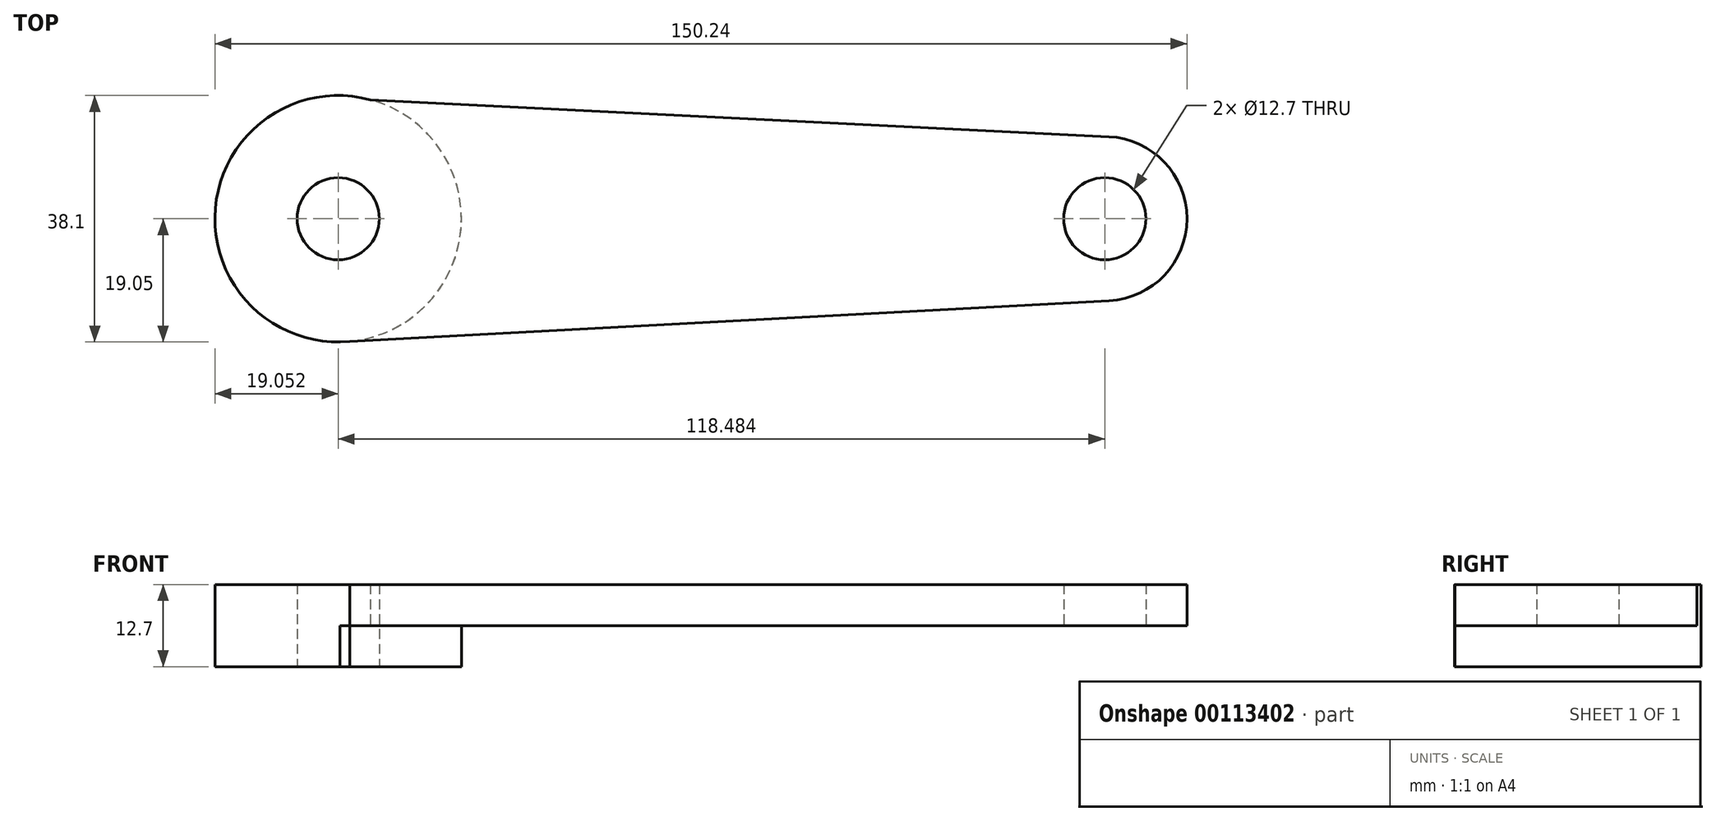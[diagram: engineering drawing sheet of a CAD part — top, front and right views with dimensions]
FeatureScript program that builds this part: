
annotation { "Feature Type Name" : "Feature", "Feature Type Description" : "" }
export const myFeature = defineFeature(function(context is Context, id is Id, definition is map)
    precondition{}
    {
        {
            var Q0;
            Q0=qCreatedBy(makeId("Top.planeOp"),FACE);
            var sketch = newSketch(context, id + "F0", { "sketchPlane" : qUnion([Q0])});
            skCircle(sketch, "E0", {"center": v(62.32, 0) * mm, "radius": 12.7 * mm});
            skCircle(sketch, "E1", {"center": v(-56.17, 0) * mm, "radius": 19.05 * mm});
            skLineSegment(sketch, "E2", {"start": v(-51.2, 18.4) * mm, "end": v(62.95, 12.68) * mm});
            skLineSegment(sketch, "E3", {"start": v(-55.91, -19.05) * mm, "end": v(63, -12.68) * mm});
            skCircle(sketch, "E4", {"center": v(-56.17, 0) * mm, "radius": 6.35 * mm});
            skCircle(sketch, "E5", {"center": v(62.32, 0) * mm, "radius": 6.35 * mm});
            skCircle(sketch, "E6", {"center": v(62.32, 0) * mm, "radius": 3.18 * mm});
            skCircle(sketch, "E7", {"center": v(-56.17, 0) * mm, "radius": 3.18 * mm});
            skSolve(sketch);
        }
        {
            var Q0;
            {var subQ0=sQuery(id+"F0.wireOp",EDGE,"E1");var subQ1=makeQuery(id+"F0.imprint","INTERSECT",VERTEX,{"derivedFrom":[subQ0,sQuery(id+"F0.wireOp",EDGE,"E2")]});Q0=makeQuery(id+"F0.imprint","IMPRINT",FACE,{"disambiguationData":[TD([[makeQuery(id+"F0.imprint","IMPRINT",EDGE,{"disambiguationData":[TD([[subQ1,-1.0]])],"derivedFrom":subQ0}),1.0]])]});}
            extrude(context, id + "F1", {"entities" : qUnion([Q0]), "endBound" : BoundingType.SYMMETRIC, "depth" : 12.7 * mm});
        }
        {
            var Q0;
            Q0 = qSketchRegion(id + "F0", true);
            var Q1;
            Q1=makeQuery(id+"F1.opExtrude","CAP_FACE",FACE,{"disambiguationData":[OSD([sQuery(id+"F0.wireOp",EDGE,"E1"),sQuery(id+"F0.wireOp",EDGE,"E3")])],"isStart":false});
            extrude(context, id + "F2", {"entities" : qUnion([Q0]), "operationType" : NewBodyOperationType.ADD, "endBound" : BoundingType.UP_TO_SURFACE, "endBoundEntityFace" : qUnion([Q1]), "depth" : 25.4 * mm});
        }
    });
